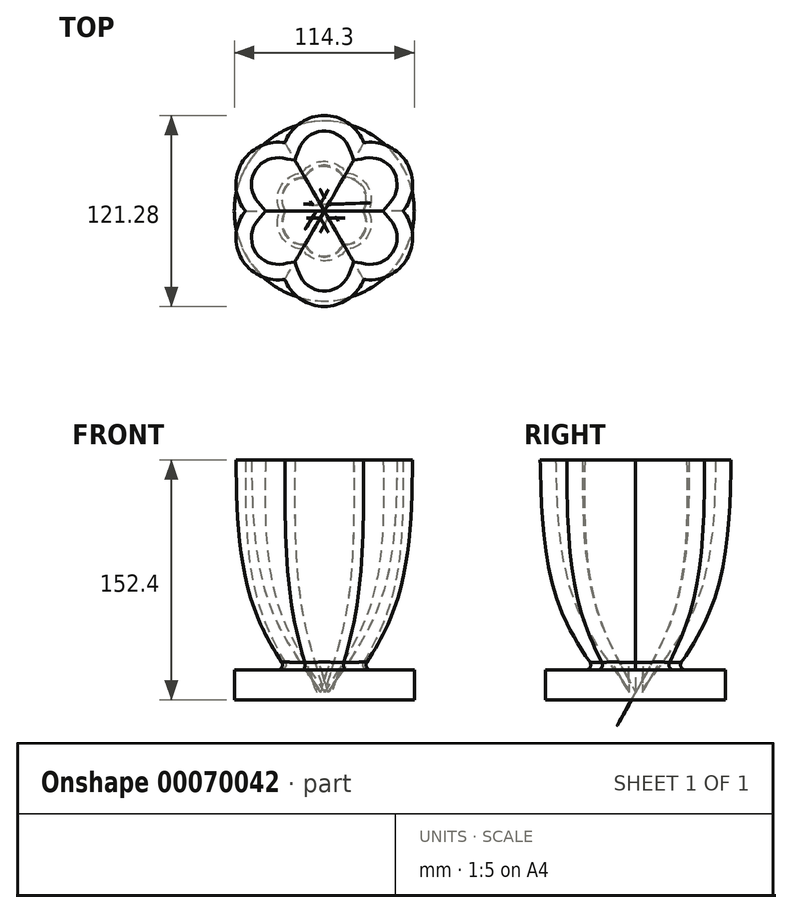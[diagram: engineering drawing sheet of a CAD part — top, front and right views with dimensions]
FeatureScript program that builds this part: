
annotation { "Feature Type Name" : "Feature", "Feature Type Description" : "" }
export const myFeature = defineFeature(function(context is Context, id is Id, definition is map)
    precondition{}
    {
        {
            var Q0;
            Q0=qCreatedBy(makeId("Top.planeOp"),FACE);
            var sketch = newSketch(context, id + "F0", { "sketchPlane" : qUnion([Q0])});
            skCircle(sketch, "E0.cCircle", {"center": v(0, 0) * mm, "radius": 29.33 * mm, "construction": true});
            skLineSegment(sketch, "E0.0", {"start": v(29.33, 16.93) * mm, "end": v(29.33, -16.93) * mm, "construction": true});
            skLineSegment(sketch, "E0.1", {"start": v(29.33, -16.93) * mm, "end": v(0, -33.87) * mm, "construction": true});
            skLineSegment(sketch, "E0.2", {"start": v(0, -33.87) * mm, "end": v(-29.33, -16.93) * mm, "construction": true});
            skLineSegment(sketch, "E0.3", {"start": v(-29.33, -16.93) * mm, "end": v(-29.33, 16.93) * mm, "construction": true});
            skLineSegment(sketch, "E0.4", {"start": v(-29.33, 16.93) * mm, "end": v(0, 33.87) * mm, "construction": true});
            skLineSegment(sketch, "E0.5", {"start": v(0, 33.87) * mm, "end": v(29.33, 16.93) * mm, "construction": true});
            skPoint(sketch, "E0.0.midPoint", {"position": v(29.33, 0) * mm});
            skArc(sketch, "E1", {"start": v(14.66, 25.4) * mm, "mid": v(0, 50.8) * mm, "end": v(-14.66, 25.4) * mm, "construction": true});
            skArc(sketch, "E2", {"start": v(29.33, 0) * mm, "mid": v(44, 25.4) * mm, "end": v(14.66, 25.4) * mm, "construction": true});
            skArc(sketch, "E3", {"start": v(14.66, -25.4) * mm, "mid": v(44, -25.4) * mm, "end": v(29.33, 0) * mm, "construction": true});
            skArc(sketch, "E4", {"start": v(-14.66, -25.4) * mm, "mid": v(0, -50.8) * mm, "end": v(14.66, -25.4) * mm, "construction": true});
            skArc(sketch, "E5", {"start": v(-29.33, 0) * mm, "mid": v(-44, -25.4) * mm, "end": v(-14.66, -25.4) * mm, "construction": true});
            skArc(sketch, "E6", {"start": v(-14.66, 25.4) * mm, "mid": v(-44, 25.4) * mm, "end": v(-29.33, 0) * mm, "construction": true});
            skLineSegment(sketch, "E7", {"start": v(0, 50.8) * mm, "end": v(0, -50.8) * mm, "construction": true});
            skArc(sketch, "E8", {"start": v(-25.04, 43.36) * mm, "mid": v(-52.52, 30.32) * mm, "end": v(-50.07, 0) * mm});
            skArc(sketch, "E9.trimOffspring", {"start": v(-50.07, 0) * mm, "mid": v(-52.52, -30.32) * mm, "end": v(-25.04, -43.36) * mm});
            skArc(sketch, "E10.trimOffspring", {"start": v(-25.04, -43.36) * mm, "mid": v(0, -60.64) * mm, "end": v(25.04, -43.36) * mm});
            skArc(sketch, "E11.trimOffspring", {"start": v(25.04, -43.36) * mm, "mid": v(52.52, -30.32) * mm, "end": v(50.07, 0) * mm});
            skArc(sketch, "E12.trimOffspring", {"start": v(50.07, 0) * mm, "mid": v(52.52, 30.32) * mm, "end": v(25.04, 43.36) * mm});
            skArc(sketch, "E13.trimOffspring", {"start": v(25.04, 43.36) * mm, "mid": v(0, 60.64) * mm, "end": v(-25.04, 43.36) * mm});
            skSolve(sketch);
        }
        {
            var Q0;
            Q0=qCreatedBy(makeId("Top.planeOp"),FACE);
            cPlane(context, id + "F1", {"entities" : qUnion([Q0]), "cplaneType" : CPlaneType.OFFSET, "offset" : 101.6 * mm, "oppositeDirection" : true, "width" : 152.4 * mm, "height" : 152.4 * mm});
        }
        {
            var Q0;
            Q0=qCreatedBy(id+"F1.planeOp",FACE);
            var sketch = newSketch(context, id + "F2", { "sketchPlane" : qUnion([Q0])});
            skCircle(sketch, "E14.cCircle", {"center": v(0, 0) * mm, "radius": 20.16 * mm, "construction": true});
            skLineSegment(sketch, "E14.0", {"start": v(20.16, 11.64) * mm, "end": v(20.16, -11.64) * mm, "construction": true});
            skLineSegment(sketch, "E14.1", {"start": v(20.16, -11.64) * mm, "end": v(0, -23.28) * mm, "construction": true});
            skLineSegment(sketch, "E14.2", {"start": v(0, -23.28) * mm, "end": v(-20.16, -11.64) * mm, "construction": true});
            skLineSegment(sketch, "E14.3", {"start": v(-20.16, -11.64) * mm, "end": v(-20.16, 11.64) * mm, "construction": true});
            skLineSegment(sketch, "E14.4", {"start": v(-20.16, 11.64) * mm, "end": v(0, 23.28) * mm, "construction": true});
            skLineSegment(sketch, "E14.5", {"start": v(0, 23.28) * mm, "end": v(20.16, 11.64) * mm, "construction": true});
            skPoint(sketch, "E14.0.midPoint", {"position": v(20.16, 0) * mm});
            skArc(sketch, "E15", {"start": v(-10.08, -17.46) * mm, "mid": v(0, -34.93) * mm, "end": v(10.08, -17.46) * mm, "construction": true});
            skArc(sketch, "E16", {"start": v(10.08, -17.46) * mm, "mid": v(30.25, -17.46) * mm, "end": v(20.16, 0) * mm, "construction": true});
            skArc(sketch, "E17", {"start": v(20.16, 0) * mm, "mid": v(30.25, 17.46) * mm, "end": v(10.08, 17.46) * mm, "construction": true});
            skArc(sketch, "E18", {"start": v(10.08, 17.46) * mm, "mid": v(0, 34.93) * mm, "end": v(-10.08, 17.46) * mm, "construction": true});
            skArc(sketch, "E19", {"start": v(-10.08, 17.46) * mm, "mid": v(-30.25, 17.46) * mm, "end": v(-20.16, 0) * mm, "construction": true});
            skArc(sketch, "E20", {"start": v(-20.16, 0) * mm, "mid": v(-30.25, -17.46) * mm, "end": v(-10.08, -17.46) * mm, "construction": true});
            skLineSegment(sketch, "E21", {"start": v(0, -34.93) * mm, "end": v(0, 34.93) * mm, "construction": true});
            skArc(sketch, "E22", {"start": v(-19.11, -33.1) * mm, "mid": v(0, -44.77) * mm, "end": v(19.11, -33.1) * mm});
            skArc(sketch, "E23", {"start": v(38.22, 0) * mm, "mid": v(38.77, 22.38) * mm, "end": v(19.11, 33.1) * mm});
            skArc(sketch, "E24.trimOffspring", {"start": v(-38.22, 0) * mm, "mid": v(-38.77, -22.38) * mm, "end": v(-19.11, -33.1) * mm});
            skArc(sketch, "E25.trimOffspring", {"start": v(19.11, -33.1) * mm, "mid": v(38.77, -22.38) * mm, "end": v(38.22, 0) * mm});
            skArc(sketch, "E26.trimOffspring", {"start": v(-19.11, 33.1) * mm, "mid": v(-38.77, 22.38) * mm, "end": v(-38.22, 0) * mm});
            skArc(sketch, "E27.trimOffspring", {"start": v(19.11, 33.1) * mm, "mid": v(0, 44.77) * mm, "end": v(-19.11, 33.1) * mm});
            skSolve(sketch);
        }
        {
            var Q0;
            Q0=qCreatedBy(makeId("Top.planeOp"),FACE);
            cPlane(context, id + "F3", {"entities" : qUnion([Q0]), "cplaneType" : CPlaneType.OFFSET, "offset" : 152.4 * mm, "oppositeDirection" : true, "width" : 152.4 * mm, "height" : 152.4 * mm});
        }
        {
            var Q0;
            Q0=qCreatedBy(id+"F3.planeOp",FACE);
            var sketch = newSketch(context, id + "F4", { "sketchPlane" : qUnion([Q0])});
            skCircle(sketch, "E28", {"center": v(0, 0) * mm, "radius": 4.92 * mm, "construction": true});
            skLineSegment(sketch, "E29.0", {"start": v(4.92, 2.84) * mm, "end": v(4.92, -2.84) * mm, "construction": true});
            skLineSegment(sketch, "E29.1", {"start": v(4.92, -2.84) * mm, "end": v(0, -5.68) * mm, "construction": true});
            skLineSegment(sketch, "E29.2", {"start": v(0, -5.68) * mm, "end": v(-4.92, -2.84) * mm, "construction": true});
            skLineSegment(sketch, "E29.3", {"start": v(-4.92, -2.84) * mm, "end": v(-4.92, 2.84) * mm, "construction": true});
            skLineSegment(sketch, "E29.4", {"start": v(-4.92, 2.84) * mm, "end": v(0, 5.68) * mm, "construction": true});
            skLineSegment(sketch, "E29.5", {"start": v(0, 5.68) * mm, "end": v(4.92, 2.84) * mm, "construction": true});
            skPoint(sketch, "E29.0.midPoint", {"position": v(4.92, 0) * mm});
            skArc(sketch, "E30", {"start": v(4.92, 8.52) * mm, "mid": v(0, 11.37) * mm, "end": v(-4.92, 8.52) * mm});
            skArc(sketch, "E31", {"start": v(9.84, 0) * mm, "mid": v(9.84, 5.68) * mm, "end": v(4.92, 8.52) * mm});
            skArc(sketch, "E32", {"start": v(4.92, -8.52) * mm, "mid": v(9.84, -5.68) * mm, "end": v(9.84, 0) * mm});
            skArc(sketch, "E33", {"start": v(-4.92, -8.52) * mm, "mid": v(0, -11.37) * mm, "end": v(4.92, -8.52) * mm});
            skArc(sketch, "E34", {"start": v(-9.84, 0) * mm, "mid": v(-9.84, -5.68) * mm, "end": v(-4.92, -8.52) * mm});
            skArc(sketch, "E35", {"start": v(-4.92, 8.52) * mm, "mid": v(-9.84, 5.68) * mm, "end": v(-9.84, 0) * mm});
            skSolve(sketch);
        }
        {
            var Q0;
            Q0=makeQuery(id+"F0.imprint","IMPRINT",FACE,{"disambiguationData":[TD([[makeQuery(id+"F0.imprint","IMPRINT",EDGE,{"derivedFrom":sQuery(id+"F0.wireOp",EDGE,"E8")}),1.0]])]});
            var Q1;
            Q1=makeQuery(id+"F2.imprint","IMPRINT",FACE,{"disambiguationData":[TD([[makeQuery(id+"F2.imprint","IMPRINT",EDGE,{"derivedFrom":sQuery(id+"F2.wireOp",EDGE,"E22")}),1.0]])]});
            var Q2;
            Q2=makeQuery(id+"F4.imprint","IMPRINT",FACE,{"disambiguationData":[TD([[makeQuery(id+"F4.imprint","IMPRINT",EDGE,{"derivedFrom":sQuery(id+"F4.wireOp",EDGE,"E30")}),1.0]])]});
            loft(context, id + "F5", {"sheetProfilesArray" : [{ "sheetProfileEntities" : qUnion([Q0]) }, { "sheetProfileEntities" : qUnion([Q1]) }, { "sheetProfileEntities" : qUnion([Q2]) }]});
        }
        {
            var Q0;
            Q0=makeQuery(id+"F5.opLoft","CAP_FACE",FACE,{"disambiguationData":[OSD([makeQuery(id+"F0.imprint","IMPRINT",FACE,{"disambiguationData":[TD([[makeQuery(id+"F0.imprint","IMPRINT",EDGE,{"derivedFrom":sQuery(id+"F0.wireOp",EDGE,"E8")}),1.0]])]})])],"isStart":true});
            shell(context, id + "F6", {"entities" : qUnion([Q0]), "thickness" : 9.84 * mm});
        }
        {
            var Q0;
            Q0=qCreatedBy(id+"F3.planeOp",FACE);
            cPlane(context, id + "F7", {"entities" : qUnion([Q0]), "cplaneType" : CPlaneType.OFFSET, "offset" : 19.05 * mm, "width" : 152.4 * mm, "height" : 152.4 * mm});
        }
        {
            var Q0;
            Q0=qCreatedBy(id+"F7.planeOp",FACE);
            var sketch = newSketch(context, id + "F8", { "sketchPlane" : qUnion([Q0])});
            skCircle(sketch, "E36.cCircle", {"center": v(0, 0) * mm, "radius": 12.7 * mm, "construction": true});
            skLineSegment(sketch, "E36.0", {"start": v(12.7, 7.33) * mm, "end": v(12.7, -7.33) * mm, "construction": true});
            skLineSegment(sketch, "E36.1", {"start": v(12.7, -7.33) * mm, "end": v(0, -14.66) * mm, "construction": true});
            skLineSegment(sketch, "E36.2", {"start": v(0, -14.66) * mm, "end": v(-12.7, -7.33) * mm, "construction": true});
            skLineSegment(sketch, "E36.3", {"start": v(-12.7, -7.33) * mm, "end": v(-12.7, 7.33) * mm, "construction": true});
            skLineSegment(sketch, "E36.4", {"start": v(-12.7, 7.33) * mm, "end": v(0, 14.66) * mm, "construction": true});
            skLineSegment(sketch, "E36.5", {"start": v(0, 14.66) * mm, "end": v(12.7, 7.33) * mm, "construction": true});
            skPoint(sketch, "E36.0.midPoint", {"position": v(12.7, 0) * mm});
            skArc(sketch, "E37", {"start": v(-9.63, 16.68) * mm, "mid": v(-21.22, 12.25) * mm, "end": v(-19.27, 0) * mm});
            skArc(sketch, "E38.trimOffspring", {"start": v(9.63, 16.68) * mm, "mid": v(0, 24.5) * mm, "end": v(-9.63, 16.68) * mm});
            skArc(sketch, "E39.trimOffspring", {"start": v(19.27, 0) * mm, "mid": v(21.22, 12.25) * mm, "end": v(9.63, 16.68) * mm});
            skArc(sketch, "E40.trimOffspring", {"start": v(9.63, -16.68) * mm, "mid": v(21.22, -12.25) * mm, "end": v(19.27, 0) * mm});
            skArc(sketch, "E41.trimOffspring", {"start": v(-9.63, -16.68) * mm, "mid": v(0, -24.5) * mm, "end": v(9.63, -16.68) * mm});
            skArc(sketch, "E42.trimOffspring", {"start": v(-19.27, 0) * mm, "mid": v(-21.22, -12.25) * mm, "end": v(-9.63, -16.68) * mm});
            skCircle(sketch, "E43", {"center": v(0, 0) * mm, "radius": 57.15 * mm});
            skSolve(sketch);
        }
        {
            var Q0;
            Q0 = qSketchRegion(id + "F8", true);
            extrude(context, id + "F9", {"entities" : qUnion([Q0]), "operationType" : NewBodyOperationType.ADD, "oppositeDirection" : true, "depth" : 19.05 * mm});
        }
        {
            var Q0;
            Q0=makeQuery(id+"F9.opExtrude","CAP_FACE",FACE,{"disambiguationData":[OSD([sQuery(id+"F8.wireOp",EDGE,"E37"),sQuery(id+"F8.wireOp",EDGE,"E38.trimOffspring"),sQuery(id+"F8.wireOp",EDGE,"E39.trimOffspring"),sQuery(id+"F8.wireOp",EDGE,"E40.trimOffspring"),sQuery(id+"F8.wireOp",EDGE,"E41.trimOffspring"),sQuery(id+"F8.wireOp",EDGE,"E42.trimOffspring"),sQuery(id+"F8.wireOp",EDGE,"E43")])],"isStart":false});
            var sketch = newSketch(context, id + "F10", { "sketchPlane" : qUnion([Q0])});
            skArc(sketch, "E44.0", {"start": v(-19.27, 0) * mm, "mid": v(-21.22, 12.25) * mm, "end": v(-9.63, 16.68) * mm});
            skArc(sketch, "E44.1", {"start": v(-9.63, 16.68) * mm, "mid": v(0, 24.5) * mm, "end": v(9.63, 16.68) * mm});
            skArc(sketch, "E44.2", {"start": v(9.63, 16.68) * mm, "mid": v(21.22, 12.25) * mm, "end": v(19.27, 0) * mm});
            skArc(sketch, "E44.3", {"start": v(19.27, 0) * mm, "mid": v(21.22, -12.25) * mm, "end": v(9.63, -16.68) * mm});
            skArc(sketch, "E44.4", {"start": v(9.63, -16.68) * mm, "mid": v(0, -24.5) * mm, "end": v(-9.63, -16.68) * mm});
            skArc(sketch, "E44.5", {"start": v(-9.63, -16.68) * mm, "mid": v(-21.22, -12.25) * mm, "end": v(-19.27, 0) * mm});
            skSolve(sketch);
        }
        {
            var Q0;
            Q0 = qSketchRegion(id + "F10", true);
            extrude(context, id + "F11", {"entities" : qUnion([Q0]), "operationType" : NewBodyOperationType.ADD, "endBound" : BoundingType.UP_TO_NEXT, "oppositeDirection" : true, "depth" : 25.4 * mm});
        }
        {
            var Q0;
            Q0=makeQuery(id+"F9.boolean.opBoolean","INTERSECT",EDGE,{"derivedFrom":[makeQuery(id+"F5.opLoft","SWEPT_FACE",FACE,{"disambiguationData":[OSD([sQuery(id+"F0.wireOp",EDGE,"E8"),sQuery(id+"F0.wireOp",EDGE,"E9.trimOffspring"),sQuery(id+"F0.wireOp",EDGE,"E13.trimOffspring"),sQuery(id+"F2.wireOp",EDGE,"E24.trimOffspring"),sQuery(id+"F2.wireOp",EDGE,"E26.trimOffspring"),sQuery(id+"F2.wireOp",EDGE,"E27.trimOffspring")])]}),makeQuery(id+"F9.opExtrude","CAP_FACE",FACE,{"disambiguationData":[OSD([sQuery(id+"F8.wireOp",EDGE,"E37"),sQuery(id+"F8.wireOp",EDGE,"E38.trimOffspring"),sQuery(id+"F8.wireOp",EDGE,"E39.trimOffspring"),sQuery(id+"F8.wireOp",EDGE,"E40.trimOffspring"),sQuery(id+"F8.wireOp",EDGE,"E41.trimOffspring"),sQuery(id+"F8.wireOp",EDGE,"E42.trimOffspring"),sQuery(id+"F8.wireOp",EDGE,"E43")])],"isStart":true})]});
            var Q1;
            Q1=makeQuery(id+"F9.boolean.opBoolean","INTERSECT",EDGE,{"derivedFrom":[makeQuery(id+"F5.opLoft","SWEPT_FACE",FACE,{"disambiguationData":[OSD([sQuery(id+"F0.wireOp",EDGE,"E8"),sQuery(id+"F0.wireOp",EDGE,"E12.trimOffspring"),sQuery(id+"F0.wireOp",EDGE,"E13.trimOffspring"),sQuery(id+"F2.wireOp",EDGE,"E23"),sQuery(id+"F2.wireOp",EDGE,"E26.trimOffspring"),sQuery(id+"F2.wireOp",EDGE,"E27.trimOffspring")])]}),makeQuery(id+"F9.opExtrude","CAP_FACE",FACE,{"disambiguationData":[OSD([sQuery(id+"F8.wireOp",EDGE,"E37"),sQuery(id+"F8.wireOp",EDGE,"E38.trimOffspring"),sQuery(id+"F8.wireOp",EDGE,"E39.trimOffspring"),sQuery(id+"F8.wireOp",EDGE,"E40.trimOffspring"),sQuery(id+"F8.wireOp",EDGE,"E41.trimOffspring"),sQuery(id+"F8.wireOp",EDGE,"E42.trimOffspring"),sQuery(id+"F8.wireOp",EDGE,"E43")])],"isStart":true})]});
            var Q2;
            Q2=makeQuery(id+"F9.boolean.opBoolean","INTERSECT",EDGE,{"derivedFrom":[makeQuery(id+"F5.opLoft","SWEPT_FACE",FACE,{"disambiguationData":[OSD([sQuery(id+"F0.wireOp",EDGE,"E11.trimOffspring"),sQuery(id+"F0.wireOp",EDGE,"E12.trimOffspring"),sQuery(id+"F0.wireOp",EDGE,"E13.trimOffspring"),sQuery(id+"F2.wireOp",EDGE,"E23"),sQuery(id+"F2.wireOp",EDGE,"E25.trimOffspring"),sQuery(id+"F2.wireOp",EDGE,"E27.trimOffspring")])]}),makeQuery(id+"F9.opExtrude","CAP_FACE",FACE,{"disambiguationData":[OSD([sQuery(id+"F8.wireOp",EDGE,"E37"),sQuery(id+"F8.wireOp",EDGE,"E38.trimOffspring"),sQuery(id+"F8.wireOp",EDGE,"E39.trimOffspring"),sQuery(id+"F8.wireOp",EDGE,"E40.trimOffspring"),sQuery(id+"F8.wireOp",EDGE,"E41.trimOffspring"),sQuery(id+"F8.wireOp",EDGE,"E42.trimOffspring"),sQuery(id+"F8.wireOp",EDGE,"E43")])],"isStart":true})]});
            var Q3;
            Q3=makeQuery(id+"F9.boolean.opBoolean","INTERSECT",EDGE,{"derivedFrom":[makeQuery(id+"F5.opLoft","SWEPT_FACE",FACE,{"disambiguationData":[OSD([sQuery(id+"F0.wireOp",EDGE,"E10.trimOffspring"),sQuery(id+"F0.wireOp",EDGE,"E11.trimOffspring"),sQuery(id+"F0.wireOp",EDGE,"E12.trimOffspring"),sQuery(id+"F2.wireOp",EDGE,"E22"),sQuery(id+"F2.wireOp",EDGE,"E23"),sQuery(id+"F2.wireOp",EDGE,"E25.trimOffspring")])]}),makeQuery(id+"F9.opExtrude","CAP_FACE",FACE,{"disambiguationData":[OSD([sQuery(id+"F8.wireOp",EDGE,"E37"),sQuery(id+"F8.wireOp",EDGE,"E38.trimOffspring"),sQuery(id+"F8.wireOp",EDGE,"E39.trimOffspring"),sQuery(id+"F8.wireOp",EDGE,"E40.trimOffspring"),sQuery(id+"F8.wireOp",EDGE,"E41.trimOffspring"),sQuery(id+"F8.wireOp",EDGE,"E42.trimOffspring"),sQuery(id+"F8.wireOp",EDGE,"E43")])],"isStart":true})]});
            var Q4;
            Q4=makeQuery(id+"F9.boolean.opBoolean","INTERSECT",EDGE,{"derivedFrom":[makeQuery(id+"F5.opLoft","SWEPT_FACE",FACE,{"disambiguationData":[OSD([sQuery(id+"F0.wireOp",EDGE,"E9.trimOffspring"),sQuery(id+"F0.wireOp",EDGE,"E10.trimOffspring"),sQuery(id+"F0.wireOp",EDGE,"E11.trimOffspring"),sQuery(id+"F2.wireOp",EDGE,"E22"),sQuery(id+"F2.wireOp",EDGE,"E24.trimOffspring"),sQuery(id+"F2.wireOp",EDGE,"E25.trimOffspring")])]}),makeQuery(id+"F9.opExtrude","CAP_FACE",FACE,{"disambiguationData":[OSD([sQuery(id+"F8.wireOp",EDGE,"E37"),sQuery(id+"F8.wireOp",EDGE,"E38.trimOffspring"),sQuery(id+"F8.wireOp",EDGE,"E39.trimOffspring"),sQuery(id+"F8.wireOp",EDGE,"E40.trimOffspring"),sQuery(id+"F8.wireOp",EDGE,"E41.trimOffspring"),sQuery(id+"F8.wireOp",EDGE,"E42.trimOffspring"),sQuery(id+"F8.wireOp",EDGE,"E43")])],"isStart":true})]});
            var Q5;
            Q5=makeQuery(id+"F9.boolean.opBoolean","INTERSECT",EDGE,{"derivedFrom":[makeQuery(id+"F5.opLoft","SWEPT_FACE",FACE,{"disambiguationData":[OSD([sQuery(id+"F0.wireOp",EDGE,"E8"),sQuery(id+"F0.wireOp",EDGE,"E9.trimOffspring"),sQuery(id+"F0.wireOp",EDGE,"E10.trimOffspring"),sQuery(id+"F2.wireOp",EDGE,"E22"),sQuery(id+"F2.wireOp",EDGE,"E24.trimOffspring"),sQuery(id+"F2.wireOp",EDGE,"E26.trimOffspring")])]}),makeQuery(id+"F9.opExtrude","CAP_FACE",FACE,{"disambiguationData":[OSD([sQuery(id+"F8.wireOp",EDGE,"E37"),sQuery(id+"F8.wireOp",EDGE,"E38.trimOffspring"),sQuery(id+"F8.wireOp",EDGE,"E39.trimOffspring"),sQuery(id+"F8.wireOp",EDGE,"E40.trimOffspring"),sQuery(id+"F8.wireOp",EDGE,"E41.trimOffspring"),sQuery(id+"F8.wireOp",EDGE,"E42.trimOffspring"),sQuery(id+"F8.wireOp",EDGE,"E43")])],"isStart":true})]});
            fillet(context, id + "F12", {"entities" : qUnion([Q0, Q1, Q2, Q3, Q4, Q5]), "radius" : 3.17 * mm, "tangentPropagation" : true, "allowEdgeOverflow" : false});
        }
    });
